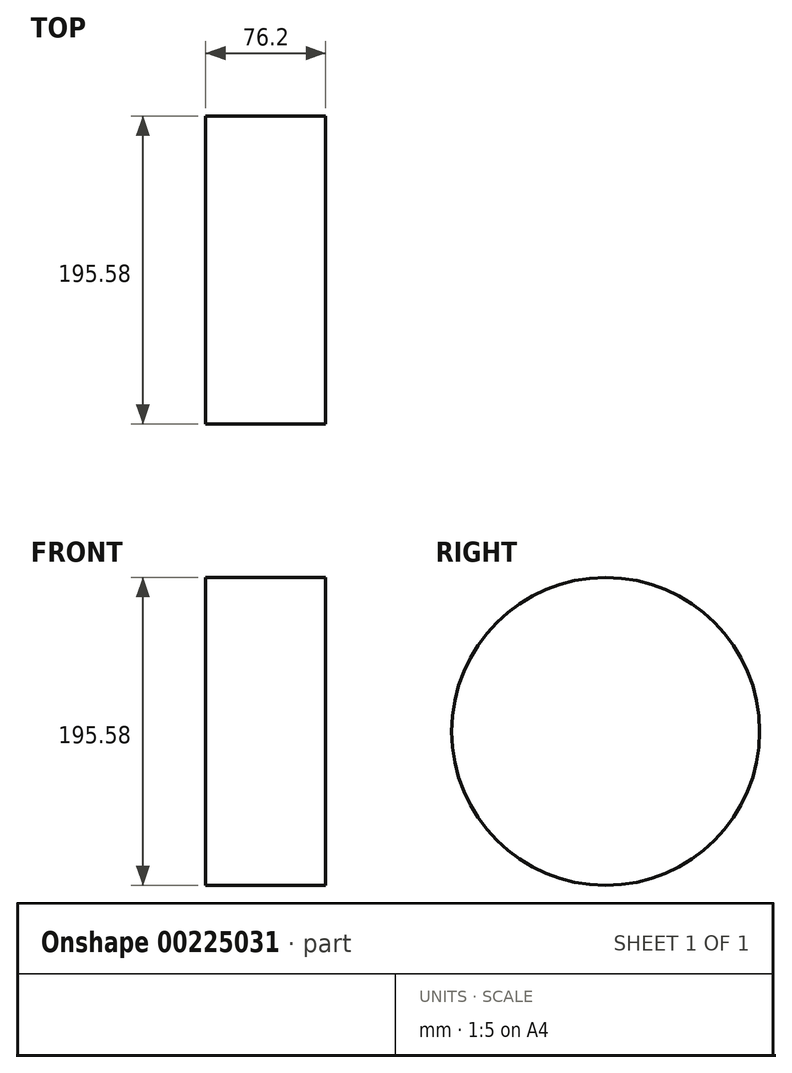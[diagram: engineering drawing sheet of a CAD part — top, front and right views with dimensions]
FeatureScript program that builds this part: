
annotation { "Feature Type Name" : "Feature", "Feature Type Description" : "" }
export const myFeature = defineFeature(function(context is Context, id is Id, definition is map)
    precondition{}
    {
        {
            var Q0;
            Q0=qCreatedBy(makeId("Front.planeOp"),FACE);
            var sketch = newSketch(context, id + "F0", { "sketchPlane" : qUnion([Q0])});
            skLineSegment(sketch, "E0", {"start": v(-186.52, 0) * mm, "end": v(-34.12, 0) * mm});
            skLineSegment(sketch, "E1.bottom", {"start": v(-38.1, 97.8) * mm, "end": v(38.1, 97.8) * mm});
            skLineSegment(sketch, "E1.top", {"start": v(-38.1, -54.6) * mm, "end": v(38.1, -54.6) * mm});
            skLineSegment(sketch, "E1.left", {"start": v(-38.1, 97.8) * mm, "end": v(-38.1, -54.6) * mm});
            skLineSegment(sketch, "E1.right", {"start": v(38.1, 97.79) * mm, "end": v(38.1, -54.6) * mm});
            skPoint(sketch, "E1.middle", {"position": v(0, 21.6) * mm});
            skLineSegment(sketch, "E2.bottom", {"start": v(-38.1, 97.8) * mm, "end": v(-20.32, 97.8) * mm});
            skLineSegment(sketch, "E2.top", {"start": v(-38.1, 127) * mm, "end": v(-20.32, 127) * mm});
            skLineSegment(sketch, "E2.left", {"start": v(-38.1, 97.8) * mm, "end": v(-38.1, 127) * mm});
            skLineSegment(sketch, "E2.right", {"start": v(-20.32, 97.8) * mm, "end": v(-20.32, 127) * mm});
            skLineSegment(sketch, "E3.MirrorCS", {"start": v(110.32, 0) * mm, "end": v(-42.08, 0) * mm});
            skLineSegment(sketch, "E4.MirrorCS", {"start": v(-38.1, -97.8) * mm, "end": v(-20.32, -97.8) * mm});
            skLineSegment(sketch, "E5.MirrorCS", {"start": v(-38.1, 54.6) * mm, "end": v(38.1, 54.6) * mm});
            skLineSegment(sketch, "E6.MirrorCS", {"start": v(38.1, -97.79) * mm, "end": v(38.1, 54.6) * mm});
            skLineSegment(sketch, "E7.MirrorCS", {"start": v(-38.1, -127) * mm, "end": v(-20.32, -127) * mm});
            skLineSegment(sketch, "E8.MirrorCS", {"start": v(-38.1, -97.8) * mm, "end": v(-38.1, -127) * mm});
            skLineSegment(sketch, "E9.MirrorCS", {"start": v(-20.32, -97.8) * mm, "end": v(-20.32, -127) * mm});
            skLineSegment(sketch, "E10.MirrorCS", {"start": v(-38.1, -97.8) * mm, "end": v(-38.1, 54.6) * mm});
            skLineSegment(sketch, "E11.MirrorCS", {"start": v(-38.1, -97.8) * mm, "end": v(38.1, -97.8) * mm});
            skPoint(sketch, "E12.MirrorP", {"position": v(0, -21.6) * mm});
            skSolve(sketch);
        }
        {
            var Q0;
            Q0=makeQuery(id+"F0.imprint","IMPRINT",FACE,{"disambiguationData":[TD([[makeQuery(id+"F0.imprint","IMPRINT",EDGE,{"derivedFrom":sQuery(id+"F0.wireOp",EDGE,"E1.bottom")}),-1.0]])]});
            var Q1;
            Q1=makeQuery(id+"F0.imprint","IMPRINT",FACE,{"disambiguationData":[TD([[makeQuery(id+"F0.imprint","IMPRINT",EDGE,{"derivedFrom":sQuery(id+"F0.wireOp",EDGE,"E2.bottom")}),1.0]])]});
            var Q2;
            {var subQ1=sQuery(id+"F0.wireOp",EDGE,"E5.MirrorCS");Q2=makeQuery(id+"F0.imprint","IMPRINT",FACE,{"disambiguationData":[TD([[makeQuery(id+"F0.imprint","IMPRINT",EDGE,{"derivedFrom":subQ1}),-1.0]])]});}
            var Q3;
            Q3=sQuery(id+"F0.wireOp",EDGE,"E3.MirrorCS");
            revolve(context, id + "F1", {"entities" : qUnion([Q0, Q1, Q2]), "axis" : qUnion([Q3]), "revolveType" : RevolveType.FULL});
        }
    });
